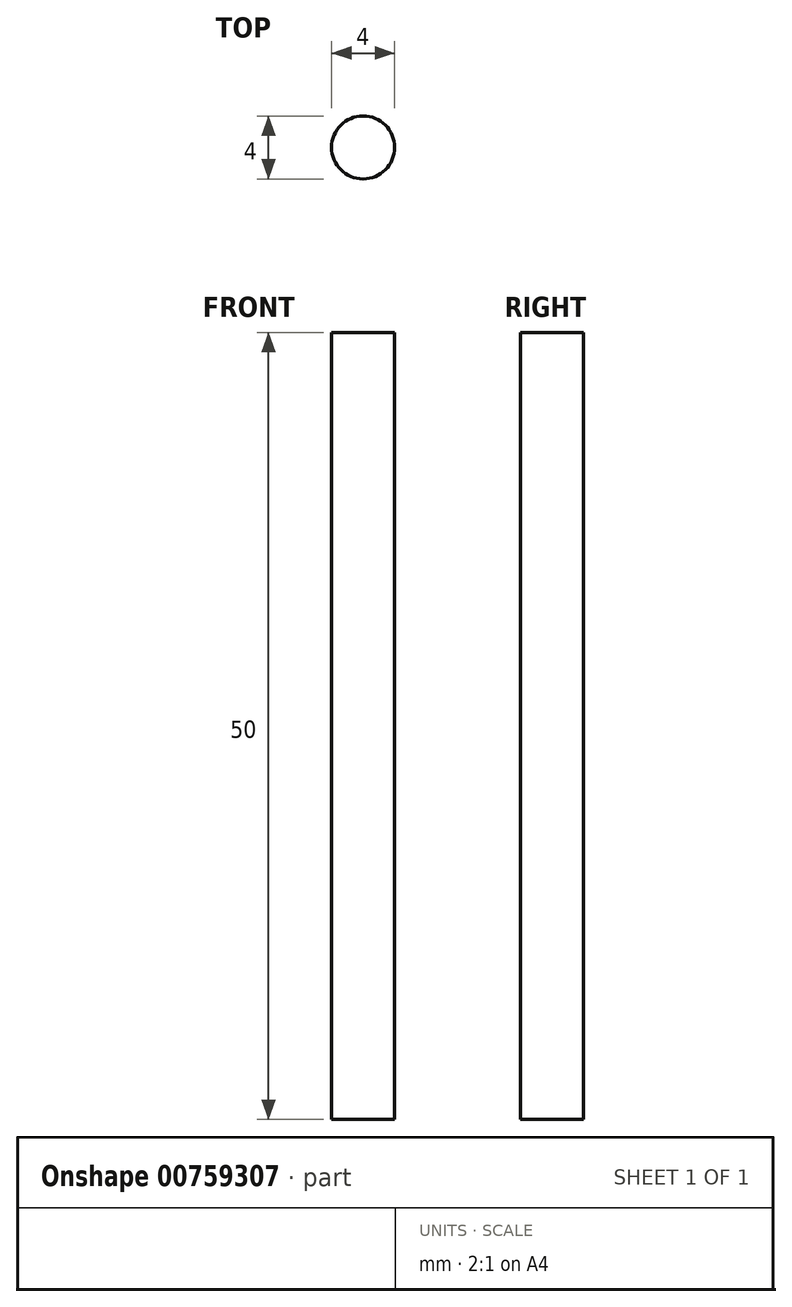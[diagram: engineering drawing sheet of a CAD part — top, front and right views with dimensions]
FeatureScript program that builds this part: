
annotation { "Feature Type Name" : "Feature", "Feature Type Description" : "" }
export const myFeature = defineFeature(function(context is Context, id is Id, definition is map)
    precondition{}
    {
        {
            var Q0;
            Q0=qCreatedBy(makeId("Top.planeOp"),FACE);
            var sketch = newSketch(context, id + "F0", { "sketchPlane" : qUnion([Q0])});
            skCircle(sketch, "E0", {"center": v(0, 0) * mm, "radius": 2 * mm});
            skSolve(sketch);
        }
        {
            var Q0;
            Q0=makeQuery(id+"F0.imprint","IMPRINT",FACE,{"disambiguationData":[TD([[makeQuery(id+"F0.imprint","IMPRINT",EDGE,{"derivedFrom":sQuery(id+"F0.wireOp",EDGE,"E0")}),1.0]])]});
            extrude(context, id + "F1", {"entities" : qUnion([Q0]), "depth" : 50 * mm, "offsetDistance" : 25 * mm});
        }
    });
